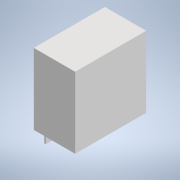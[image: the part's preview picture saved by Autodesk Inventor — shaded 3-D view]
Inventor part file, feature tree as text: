
AUTODESK INVENTOR PART (.ipt)
format: ipt  version: 2022 (Build 260153000, 153)  size: 102,400 bytes
history: native  units: mm
features: extrude x2, sketch x2, other x1
ambient origin geometry x8: Origin, YZ Plane, XZ Plane, XY Plane, X Axis, Y Axis, Z Axis, Center Point
bodies: Body1 (feature_tree)
feature tree (5):
  other  "Твердое тело1"
  extrude  "Выдавливание1"  Depth=8.5mm
  extrude  "Выдавливание2"  Depth=8.5mm
  sketch  "Эскиз1"
  sketch  "Эскиз2"
